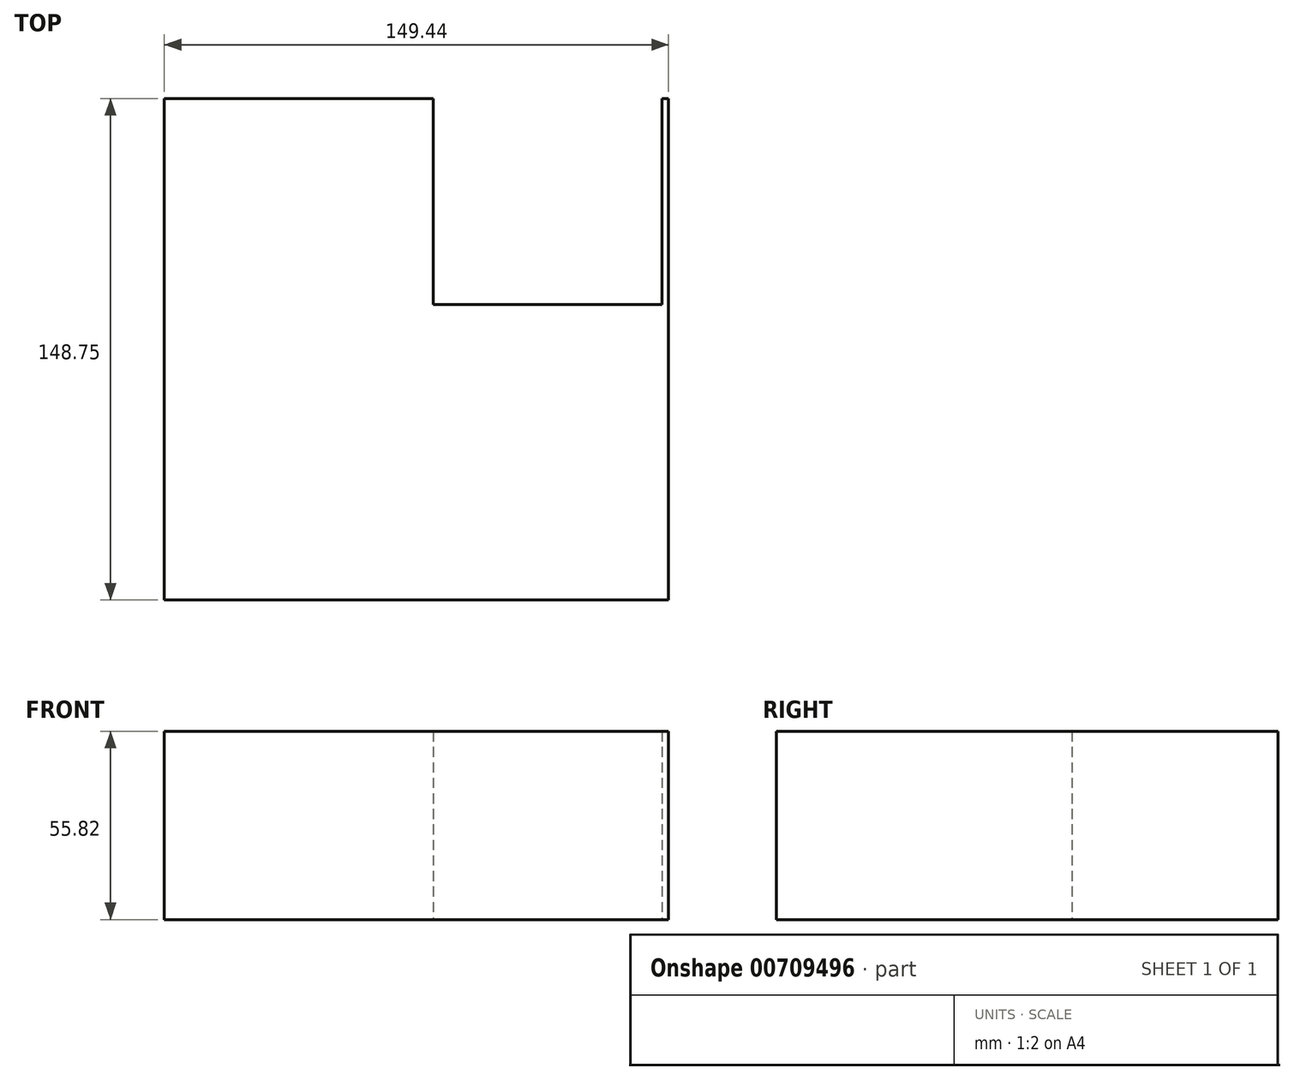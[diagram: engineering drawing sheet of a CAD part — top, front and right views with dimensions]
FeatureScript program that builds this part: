
annotation { "Feature Type Name" : "Feature", "Feature Type Description" : "" }
export const myFeature = defineFeature(function(context is Context, id is Id, definition is map)
    precondition{}
    {
        {
            var Q0;
            Q0=qCreatedBy(makeId("Top.planeOp"),FACE);
            var sketch = newSketch(context, id + "F0", { "sketchPlane" : qUnion([Q0])});
            skLineSegment(sketch, "E0.bottom", {"start": v(-74.72, 0) * mm, "end": v(74.72, 0) * mm});
            skLineSegment(sketch, "E0.top", {"start": v(-74.72, -148.75) * mm, "end": v(74.72, -148.75) * mm});
            skLineSegment(sketch, "E0.left", {"start": v(-74.72, 0) * mm, "end": v(-74.72, -148.75) * mm});
            skLineSegment(sketch, "E0.right", {"start": v(74.72, 0) * mm, "end": v(74.72, -148.75) * mm});
            skPoint(sketch, "E0.middle", {"position": v(0, -74.37) * mm});
            skLineSegment(sketch, "E1.bottom", {"start": v(-74.72, 0) * mm, "end": v(-40.94, 0) * mm});
            skLineSegment(sketch, "E1.top", {"start": v(-74.72, 91.93) * mm, "end": v(-40.94, 91.93) * mm});
            skLineSegment(sketch, "E1.left", {"start": v(-74.72, 0) * mm, "end": v(-74.72, 91.93) * mm});
            skLineSegment(sketch, "E1.right", {"start": v(-40.94, 0) * mm, "end": v(-40.94, 91.93) * mm});
            skPoint(sketch, "E1.middle", {"position": v(-57.83, 45.97) * mm});
            skLineSegment(sketch, "E2.bottom", {"start": v(72.73, 61.18) * mm, "end": v(5.03, 61.18) * mm});
            skLineSegment(sketch, "E2.top", {"start": v(72.73, -61.18) * mm, "end": v(5.03, -61.18) * mm});
            skLineSegment(sketch, "E2.left", {"start": v(72.73, 61.18) * mm, "end": v(72.73, -61.18) * mm});
            skLineSegment(sketch, "E2.right", {"start": v(5.03, 61.18) * mm, "end": v(5.03, -61.18) * mm});
            skPoint(sketch, "E2.middle", {"position": v(38.88, 0) * mm});
            skSolve(sketch);
        }
        {
            var Q0;
            Q0=makeQuery(id+"F0.imprint","IMPRINT",FACE,{"disambiguationData":[TD([[makeQuery(id+"F0.imprint","IMPRINT",EDGE,{"derivedFrom":sQuery(id+"F0.wireOp",EDGE,"E0.top")}),1.0]])]});
            var sketch = newSketch(context, id + "F1", { "sketchPlane" : qUnion([Q0])});
            skSolve(sketch);
        }
        {
            var Q0;
            Q0=makeQuery(id+"F1.imprint","IMPRINT",FACE,{"disambiguationData":[TD([[makeQuery(id+"F1.imprint","IMPRINT",EDGE,{"derivedFrom":makeQuery(id+"F0.imprint","IMPRINT",EDGE,{"derivedFrom":sQuery(id+"F0.wireOp",EDGE,"E0.top")})}),1.0]])]});
            extrude(context, id + "F2", {"entities" : qUnion([Q0]), "depth" : 55.82 * mm, "offsetDistance" : 25.4 * mm});
        }
    });
